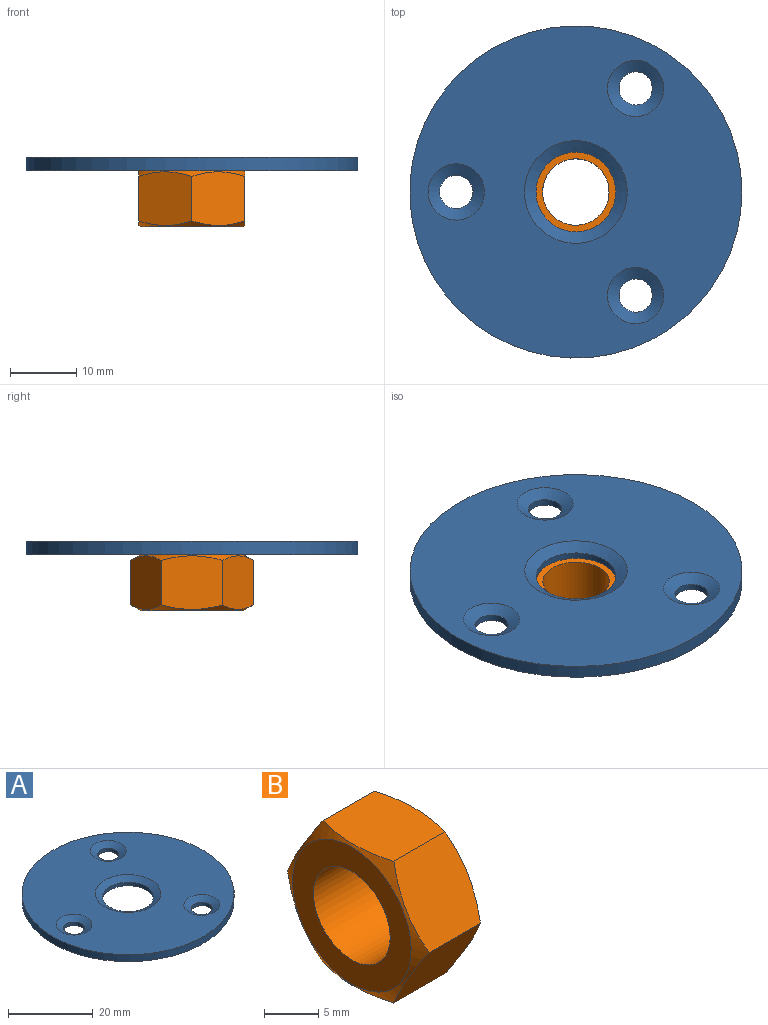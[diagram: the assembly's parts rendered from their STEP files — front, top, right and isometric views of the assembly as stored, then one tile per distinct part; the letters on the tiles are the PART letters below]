
ASSEMBLY  parts=2 mates=1
PART A: 11 faces, bbox 50x50x2 mm
  f0: cylinder r=6mm len=12mm, axis (0,0,-1), area 37.7mm2, adj f6,f7
  f1: cylinder r=2.5mm len=5mm, axis (0,0,-1), area 15.7mm2, adj f6,f10
  f2: cylinder r=2.5mm len=5mm, axis (0,0,-1), area 15.7mm2, adj f6,f8
  f3: cylinder r=2.5mm len=5mm, axis (0,0,-1), area 15.7mm2, adj f6,f9
  f4: cylinder r=25mm len=50mm, axis (0,0,-1), area 314.2mm2, adj f5,f6
  f5: plane 50x50mm, normal (0,0,1), area 1606.9mm2, adj f4,f7,f8,f9,f10
  f6: plane 50x50mm, normal (0,0,-1), area 1791.5mm2, adj f0,f1,f2,f3,f4
  f7: cone r=6mm half-angle=60deg, axis (0,0,1), area 86.3mm2, adj f0,f5
  f8: cone r=2.5mm half-angle=60deg, axis (0,0,1), area 42.3mm2, adj f2,f5
  f9: cone r=2.5mm half-angle=60deg, axis (0,0,1), area 42.3mm2, adj f3,f5
  f10: cone r=2.5mm half-angle=60deg, axis (0,0,1), area 42.3mm2, adj f1,f5
PART B: 11 faces, bbox 8.4x18.5x18.5 mm
  f0: plane 15.48x15.48mm, normal (1,0,0), area 109.5mm2, adj f1,f4
  f1: cylinder r=5mm len=10mm, axis (-1,0,0), area 263.9mm2, adj f0,f2
  f2: plane 15.48x15.48mm, normal (-1,0,0), area 109.5mm2, adj f1,f3
  f3: cone r=7.74mm half-angle=60deg, axis (1,0,0), area 38.8mm2, adj f2,f5,f6,f7,f8,f9,f10
  f4: cone r=7.74mm half-angle=60deg, axis (-1,0,0), area 38.8mm2, adj f0,f5,f6,f7,f8,f9,f10
  f5: plane 8.11x8mm, normal (0,-0.87,-0.5), area 70.3mm2, adj f3,f4,f6,f10
  f6: plane 8.11x8mm, normal (0,-0.87,0.5), area 70.3mm2, adj f3,f4,f5,f7
  f7: plane 9.25x8.1mm, normal (0,0,1), area 70.3mm2, adj f3,f4,f6,f8
  f8: plane 8.11x8mm, normal (0,0.87,0.5), area 70.3mm2, adj f3,f4,f7,f9
  f9: plane 8.11x8mm, normal (0,0.87,-0.5), area 70.3mm2, adj f3,f4,f8,f10
  f10: plane 9.25x8.1mm, normal (0,0,-1), area 70.3mm2, adj f3,f4,f5,f9
PLACE A at identity
PLACE B rot(axis=(0,-1,0),90deg) t=(0,0,-8.4)mm
MATE fastened B.f1 <-> A.f0  axis (0,0,1) through (0,0,0)mm
